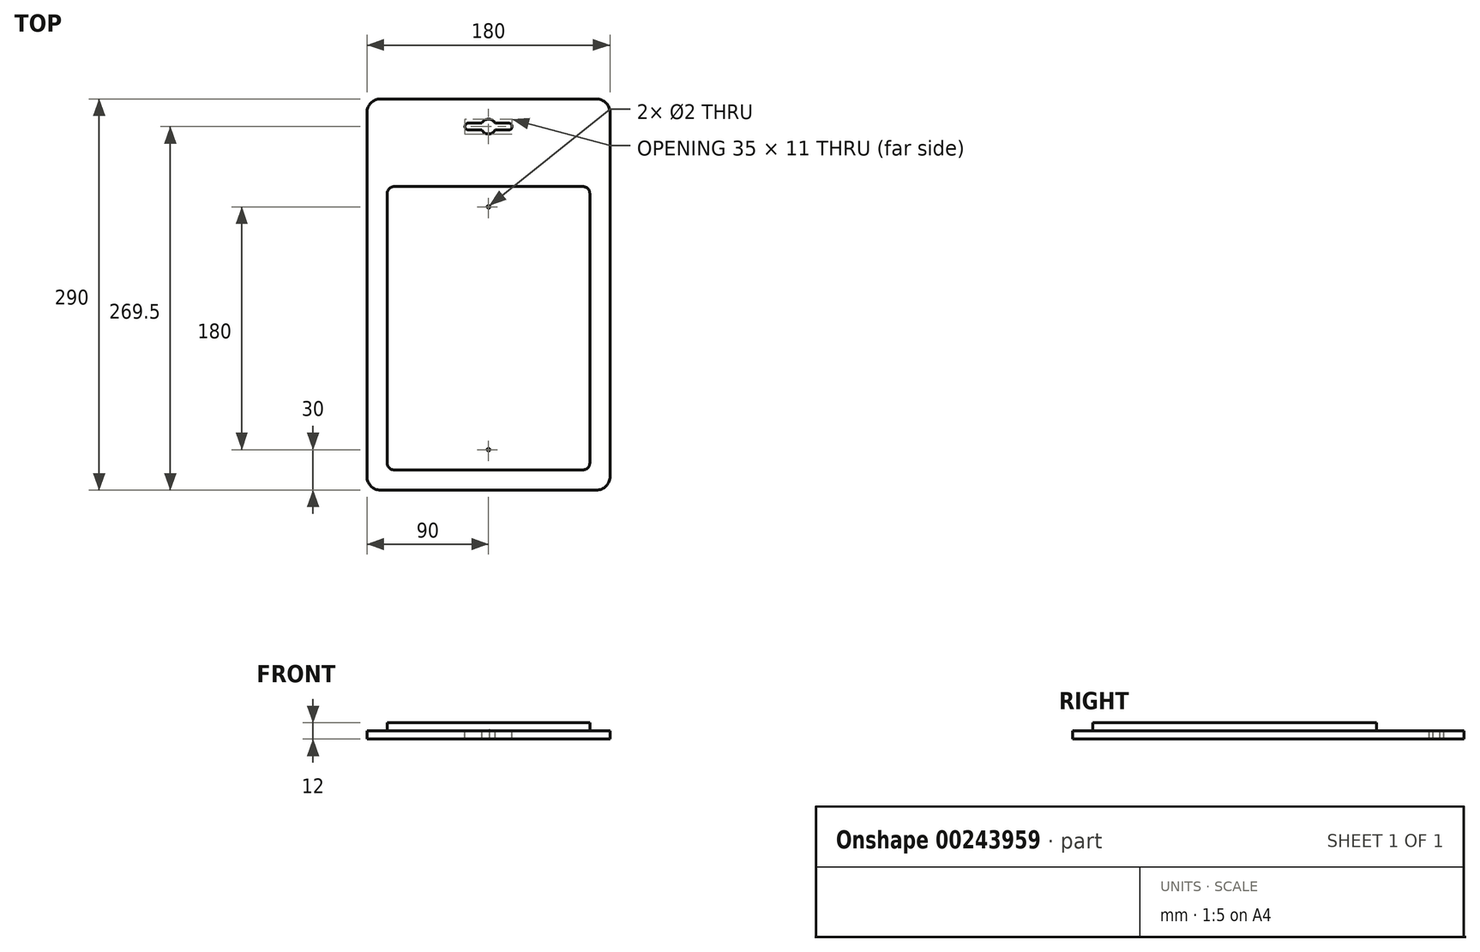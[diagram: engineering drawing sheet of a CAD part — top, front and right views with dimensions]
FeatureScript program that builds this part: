
annotation { "Feature Type Name" : "Feature", "Feature Type Description" : "" }
export const myFeature = defineFeature(function(context is Context, id is Id, definition is map)
    precondition{}
    {
        {
            var Q0;
            Q0=qCreatedBy(makeId("Top.planeOp"),FACE);
            var sketch = newSketch(context, id + "F0", { "sketchPlane" : qUnion([Q0])});
            skLineSegment(sketch, "E0.bottom", {"start": v(70, 105) * mm, "end": v(-70, 105) * mm});
            skLineSegment(sketch, "E0.top", {"start": v(70, -105) * mm, "end": v(-70, -105) * mm});
            skLineSegment(sketch, "E0.left", {"start": v(75, 100) * mm, "end": v(75, -100) * mm});
            skLineSegment(sketch, "E0.right", {"start": v(-75, 100) * mm, "end": v(-75, -100) * mm});
            skPoint(sketch, "E0.middle", {"position": v(0, 0) * mm});
            skPoint(sketch, "E1.visualSharp", {"position": v(-75, 105) * mm});
            skArc(sketch, "E1.filletArc", {"start": v(-70, 105) * mm, "mid": v(-73.54, 103.54) * mm, "end": v(-75, 100) * mm});
            skPoint(sketch, "E2.visualSharp", {"position": v(75, 105) * mm});
            skArc(sketch, "E2.filletArc", {"start": v(75, 100) * mm, "mid": v(73.54, 103.54) * mm, "end": v(70, 105) * mm});
            skPoint(sketch, "E3.visualSharp", {"position": v(-75, -105) * mm});
            skArc(sketch, "E3.filletArc", {"start": v(-75, -100) * mm, "mid": v(-73.54, -103.54) * mm, "end": v(-70, -105) * mm});
            skPoint(sketch, "E4.visualSharp", {"position": v(75, -105) * mm});
            skArc(sketch, "E4.filletArc", {"start": v(70, -105) * mm, "mid": v(73.54, -103.54) * mm, "end": v(75, -100) * mm});
            skSolve(sketch);
        }
        {
            var Q0;
            Q0 = qSketchRegion(id + "F0", true);
            extrude(context, id + "F1", {"entities" : qUnion([Q0]), "depth" : 6 * mm});
        }
        {
            var Q0;
            Q0=makeQuery(id+"F1.opExtrude","CAP_FACE",FACE,{"disambiguationData":[OSD([sQuery(id+"F0.wireOp",EDGE,"E0.bottom"),sQuery(id+"F0.wireOp",EDGE,"E0.top"),sQuery(id+"F0.wireOp",EDGE,"E0.left"),sQuery(id+"F0.wireOp",EDGE,"E0.right"),sQuery(id+"F0.wireOp",EDGE,"E1.filletArc"),sQuery(id+"F0.wireOp",EDGE,"E2.filletArc"),sQuery(id+"F0.wireOp",EDGE,"E3.filletArc"),sQuery(id+"F0.wireOp",EDGE,"E4.filletArc")])],"isStart":true});
            var sketch = newSketch(context, id + "F2", { "sketchPlane" : qUnion([Q0])});
            skLineSegment(sketch, "E5.bottom", {"start": v(-90, -120) * mm, "end": v(90, -120) * mm});
            skLineSegment(sketch, "E5.top", {"start": v(-90, 120) * mm, "end": v(90, 120) * mm});
            skLineSegment(sketch, "E5.left", {"start": v(-90, -120) * mm, "end": v(-90, 120) * mm});
            skLineSegment(sketch, "E5.right", {"start": v(90, -120) * mm, "end": v(90, 120) * mm});
            skPoint(sketch, "E5.middle", {"position": v(0, 0) * mm});
            skSolve(sketch);
        }
        {
            var Q0;
            Q0=makeQuery(id+"F2.imprint","IMPRINT",FACE,{"disambiguationData":[TD([[makeQuery(id+"F2.imprint","IMPRINT",EDGE,{"derivedFrom":sQuery(id+"F2.wireOp",EDGE,"E5.bottom")}),1.0]])]});
            var Q1;
            Q1=makeQuery(id+"F2.imprint","IMPRINT",FACE,{"disambiguationData":[TD([[makeQuery(id+"F2.imprint","IMPRINT",EDGE,{"derivedFrom":makeQuery(id+"F1.opExtrude","CAP_EDGE",EDGE,{"disambiguationData":[OSD([sQuery(id+"F0.wireOp",EDGE,"E0.bottom")])],"isStart":true})}),-1.0]])]});
            extrude(context, id + "F3", {"entities" : qUnion([Q0, Q1]), "operationType" : NewBodyOperationType.ADD, "depth" : 6 * mm});
        }
        {
            var Q0;
            Q0=makeQuery(id+"F3.opExtrude","CAP_FACE",FACE,{"disambiguationData":[OSD([sQuery(id+"F2.wireOp",EDGE,"E5.bottom"),sQuery(id+"F2.wireOp",EDGE,"E5.top"),sQuery(id+"F2.wireOp",EDGE,"E5.left"),sQuery(id+"F2.wireOp",EDGE,"E5.right")])],"isStart":true});
            var sketch = newSketch(context, id + "F4", { "sketchPlane" : qUnion([Q0])});
            skLineSegment(sketch, "E6.bottom", {"start": v(-90, 120) * mm, "end": v(90, 120) * mm});
            skLineSegment(sketch, "E6.top", {"start": v(-90, 170) * mm, "end": v(90, 170) * mm});
            skLineSegment(sketch, "E6.left", {"start": v(-90, 120) * mm, "end": v(-90, 170) * mm});
            skLineSegment(sketch, "E6.right", {"start": v(90, 120) * mm, "end": v(90, 170) * mm});
            skSolve(sketch);
        }
        {
            var Q0;
            Q0=makeQuery(id+"F4.imprint","IMPRINT",FACE,{"disambiguationData":[TD([[makeQuery(id+"F4.imprint","IMPRINT",EDGE,{"derivedFrom":sQuery(id+"F4.wireOp",EDGE,"E6.bottom")}),1.0]])]});
            extrude(context, id + "F5", {"entities" : qUnion([Q0]), "operationType" : NewBodyOperationType.ADD, "oppositeDirection" : true, "depth" : 6 * mm});
        }
        {
            var Q0;
            Q0=makeQuery(id+"F5.opExtrude","SWEPT_EDGE",EDGE,{"disambiguationData":[OSD([sQuery(id+"F4.wireOp",EDGE,"E6.top"),sQuery(id+"F4.wireOp",EDGE,"E6.left")])]});
            var Q1;
            Q1=makeQuery(id+"F5.opExtrude","SWEPT_EDGE",EDGE,{"disambiguationData":[OSD([sQuery(id+"F4.wireOp",EDGE,"E6.top"),sQuery(id+"F4.wireOp",EDGE,"E6.right")])]});
            var Q2;
            Q2=makeQuery(id+"F3.opExtrude","SWEPT_EDGE",EDGE,{"disambiguationData":[OSD([sQuery(id+"F2.wireOp",EDGE,"E5.top"),sQuery(id+"F2.wireOp",EDGE,"E5.left")])]});
            var Q3;
            Q3=makeQuery(id+"F3.opExtrude","SWEPT_EDGE",EDGE,{"disambiguationData":[OSD([sQuery(id+"F2.wireOp",EDGE,"E5.top"),sQuery(id+"F2.wireOp",EDGE,"E5.right")])]});
            fillet(context, id + "F6", {"entities" : qUnion([Q0, Q1, Q2, Q3]), "radius" : 10.1 * mm, "tangentPropagation" : true, "allowEdgeOverflow" : false});
        }
        {
            var Q0;
            Q0=makeQuery(id+"F5.boolean.opBoolean","MERGE",FACE,{"derivedFrom":[makeQuery(id+"F3.opExtrude","CAP_FACE",FACE,{"disambiguationData":[OSD([sQuery(id+"F2.wireOp",EDGE,"E5.bottom"),sQuery(id+"F2.wireOp",EDGE,"E5.top"),sQuery(id+"F2.wireOp",EDGE,"E5.left"),sQuery(id+"F2.wireOp",EDGE,"E5.right")])],"isStart":true}),makeQuery(id+"F5.opExtrude","CAP_FACE",FACE,{"disambiguationData":[OSD([sQuery(id+"F4.wireOp",EDGE,"E6.bottom"),sQuery(id+"F4.wireOp",EDGE,"E6.top"),sQuery(id+"F4.wireOp",EDGE,"E6.left"),sQuery(id+"F4.wireOp",EDGE,"E6.right")])],"isStart":true})]});
            var sketch = newSketch(context, id + "F7", { "sketchPlane" : qUnion([Q0])});
            skLineSegment(sketch, "E7", {"start": v(0, 170) * mm, "end": v(0, 155) * mm, "construction": true});
            skPoint(sketch, "E7.endSnap0", {"position": v(0, 170) * mm});
            skLineSegment(sketch, "E8", {"start": v(0, 155) * mm, "end": v(0, 144) * mm, "construction": true});
            skCircle(sketch, "E9", {"center": v(0, 149.5) * mm, "radius": 5.5 * mm});
            skLineSegment(sketch, "E10.bottom", {"start": v(15, 152) * mm, "end": v(-15, 152) * mm});
            skLineSegment(sketch, "E10.top", {"start": v(15, 147) * mm, "end": v(-15, 147) * mm});
            skLineSegment(sketch, "E10.left", {"start": v(17.5, 149.5) * mm, "end": v(17.5, 149.5) * mm});
            skLineSegment(sketch, "E10.right", {"start": v(-17.5, 149.5) * mm, "end": v(-17.5, 149.5) * mm});
            skPoint(sketch, "E11.visualSharp", {"position": v(-17.5, 152) * mm});
            skArc(sketch, "E11.filletArc", {"start": v(-15, 152) * mm, "mid": v(-16.77, 151.27) * mm, "end": v(-17.5, 149.5) * mm});
            skPoint(sketch, "E12.visualSharp", {"position": v(-17.5, 147) * mm});
            skArc(sketch, "E12.filletArc", {"start": v(-17.5, 149.5) * mm, "mid": v(-16.77, 147.73) * mm, "end": v(-15, 147) * mm});
            skPoint(sketch, "E13.visualSharp", {"position": v(17.5, 152) * mm});
            skArc(sketch, "E13.filletArc", {"start": v(17.5, 149.5) * mm, "mid": v(16.77, 151.27) * mm, "end": v(15, 152) * mm});
            skPoint(sketch, "E14.visualSharp", {"position": v(17.5, 147) * mm});
            skArc(sketch, "E14.filletArc", {"start": v(15, 147) * mm, "mid": v(16.77, 147.73) * mm, "end": v(17.5, 149.5) * mm});
            skSolve(sketch);
        }
        {
            var Q0;
            Q0 = qSketchRegion(id + "F7", true);
            extrude(context, id + "F8", {"entities" : qUnion([Q0]), "operationType" : NewBodyOperationType.REMOVE, "oppositeDirection" : true, "depth" : 25 * mm});
        }
        {
            var Q0;
            Q0=makeQuery(id+"F1.opExtrude","CAP_FACE",FACE,{"disambiguationData":[OSD([sQuery(id+"F0.wireOp",EDGE,"E0.bottom"),sQuery(id+"F0.wireOp",EDGE,"E0.top"),sQuery(id+"F0.wireOp",EDGE,"E0.left"),sQuery(id+"F0.wireOp",EDGE,"E0.right"),sQuery(id+"F0.wireOp",EDGE,"E1.filletArc"),sQuery(id+"F0.wireOp",EDGE,"E2.filletArc"),sQuery(id+"F0.wireOp",EDGE,"E3.filletArc"),sQuery(id+"F0.wireOp",EDGE,"E4.filletArc")])],"isStart":false});
            var sketch = newSketch(context, id + "F9", { "sketchPlane" : qUnion([Q0])});
            skLineSegment(sketch, "E15", {"start": v(0, 105) * mm, "end": v(0, 90) * mm, "construction": true});
            skPoint(sketch, "E15.endSnap0", {"position": v(0, -105) * mm});
            skCircle(sketch, "E16", {"center": v(0, 90) * mm, "radius": 1 * mm});
            skLineSegment(sketch, "E17", {"start": v(-75, 0) * mm, "end": v(-46.75, 0) * mm, "construction": true});
            skPoint(sketch, "E17.endSnap0", {"position": v(-75, 0) * mm});
            skCircle(sketch, "E18.MirrorC", {"center": v(0, -90) * mm, "radius": 1 * mm});
            skSolve(sketch);
        }
        {
            var Q0;
            Q0 = qSketchRegion(id + "F9", true);
            extrude(context, id + "F10", {"entities" : qUnion([Q0]), "operationType" : NewBodyOperationType.REMOVE, "oppositeDirection" : true, "depth" : 25 * mm});
        }
    });
